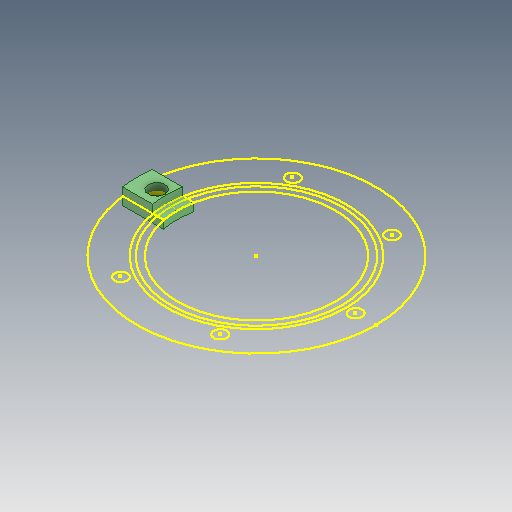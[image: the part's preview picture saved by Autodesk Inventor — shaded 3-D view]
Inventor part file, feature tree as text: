
AUTODESK INVENTOR PART (.ipt)
format: ipt  version: 2020.3 (Build 243373000, 373)  size: 97,280 bytes
history: native  units: mm
features: other x3, sketch x1
ambient origin geometry x8: Origin, YZ Plane, XZ Plane, XY Plane, X Axis, Y Axis, Z Axis, Center Point
bodies: Solid1 (feature_tree)
feature tree (4):
  other  "ClipsForLens.ipt"
  other  "Solid1::ClipsForLens.ipt"
  other  "TaggingFeature1"
  sketch  "Sketch2"  dims[d0=10.0mm]
